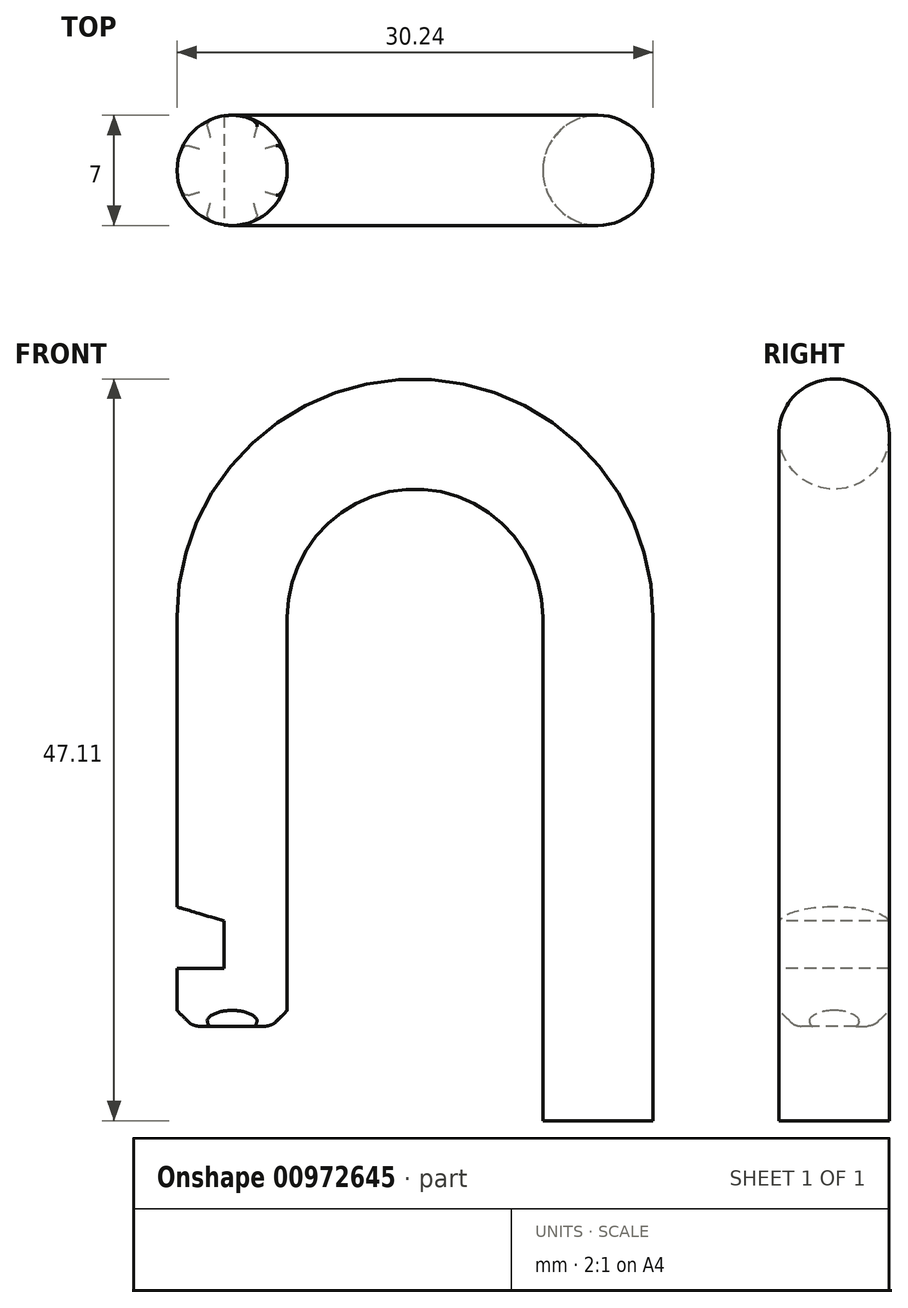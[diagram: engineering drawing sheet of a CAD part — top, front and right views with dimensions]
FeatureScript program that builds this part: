
annotation { "Feature Type Name" : "Feature", "Feature Type Description" : "" }
export const myFeature = defineFeature(function(context is Context, id is Id, definition is map)
    precondition{}
    {
        {
            var Q0;
            Q0=qCreatedBy(makeId("Front.planeOp"),FACE);
            var sketch = newSketch(context, id + "F0", { "sketchPlane" : qUnion([Q0])});
            skArc(sketch, "E0", {"start": v(8.12, 0) * mm, "mid": v(0, 8.12) * mm, "end": v(-8.12, 0) * mm});
            skLineSegment(sketch, "E1", {"start": v(15.12, 0) * mm, "end": v(15.12, -32) * mm});
            skLineSegment(sketch, "E2", {"start": v(-15.12, 0) * mm, "end": v(-15.11, -18.42) * mm});
            skArc(sketch, "E3", {"start": v(15.12, 0) * mm, "mid": v(0, 15.12) * mm, "end": v(-15.12, 0) * mm});
            skLineSegment(sketch, "E4.trimOffspring", {"start": v(-8.12, 0) * mm, "end": v(-8.11, -25) * mm});
            skLineSegment(sketch, "E5.trimOffspring", {"start": v(8.12, 0) * mm, "end": v(8.12, -32) * mm});
            skLineSegment(sketch, "E6", {"start": v(8.12, -32) * mm, "end": v(15.12, -32) * mm});
            skLineSegment(sketch, "E7.top", {"start": v(-12.11, -22.32) * mm, "end": v(-15.11, -22.32) * mm});
            skLineSegment(sketch, "E7.left", {"start": v(-12.11, -19.32) * mm, "end": v(-12.11, -22.32) * mm});
            skLineSegment(sketch, "E8", {"start": v(-12.11, -19.32) * mm, "end": v(-15.11, -18.42) * mm});
            skLineSegment(sketch, "E9.bottom", {"start": v(-15.11, -25) * mm, "end": v(-8.11, -25) * mm});
            skLineSegment(sketch, "E9.top", {"start": v(-15.11, -26) * mm, "end": v(-8.11, -26) * mm});
            skLineSegment(sketch, "E9.left", {"start": v(-15.11, -25) * mm, "end": v(-15.11, -26) * mm});
            skLineSegment(sketch, "E9.right", {"start": v(-8.11, -25) * mm, "end": v(-8.11, -26) * mm});
            skLineSegment(sketch, "E10.trimOffspring", {"start": v(-15.11, -22.32) * mm, "end": v(-15.11, -25) * mm});
            skSolve(sketch);
        }
        {
            var Q0;
            Q0 = qSketchRegion(id + "F0", true);
            extrude(context, id + "F1", {"entities" : qUnion([Q0]), "oppositeDirection" : true, "depth" : 7 * mm, "offsetDistance" : 25 * mm});
        }
        {
            var Q0;
            Q0=makeQuery(id+"F1.opExtrude","SWEPT_EDGE",EDGE,{"disambiguationData":[OSD([sQuery(id+"F0.wireOp",EDGE,"E9.top"),sQuery(id+"F0.wireOp",EDGE,"E9.right")])]});
            var Q1;
            Q1=makeQuery(id+"F1.opExtrude","CAP_EDGE",EDGE,{"disambiguationData":[OSD([sQuery(id+"F0.wireOp",EDGE,"E9.top")])],"isStart":true});
            var Q2;
            Q2=makeQuery(id+"F1.opExtrude","CAP_EDGE",EDGE,{"disambiguationData":[OSD([sQuery(id+"F0.wireOp",EDGE,"E9.top")])],"isStart":false});
            var Q3;
            Q3=makeQuery(id+"F1.opExtrude","SWEPT_EDGE",EDGE,{"disambiguationData":[OSD([sQuery(id+"F0.wireOp",EDGE,"E9.top"),sQuery(id+"F0.wireOp",EDGE,"E9.left")])]});
            chamfer(context, id + "F2", {"entities" : qUnion([Q0, Q1, Q2, Q3]), "width" : 1 * mm, "tangentPropagation" : true});
        }
        {
            var Q0;
            Q0=makeQuery(id+"F1.opExtrude","CAP_EDGE",EDGE,{"disambiguationData":[OSD([sQuery(id+"F0.wireOp",EDGE,"E5.trimOffspring")])],"isStart":true});
            var Q1;
            Q1=makeQuery(id+"F1.opExtrude","CAP_EDGE",EDGE,{"disambiguationData":[OSD([sQuery(id+"F0.wireOp",EDGE,"E1")])],"isStart":true});
            var Q2;
            Q2=makeQuery(id+"F1.opExtrude","CAP_EDGE",EDGE,{"disambiguationData":[OSD([sQuery(id+"F0.wireOp",EDGE,"E1")])],"isStart":false});
            var Q3;
            Q3=makeQuery(id+"F1.opExtrude","CAP_EDGE",EDGE,{"disambiguationData":[OSD([sQuery(id+"F0.wireOp",EDGE,"E5.trimOffspring")])],"isStart":false});
            fillet(context, id + "F3", {"entities" : qUnion([Q0, Q1, Q2, Q3]), "radius" : 3.5 * mm, "tangentPropagation" : true, "allowEdgeOverflow" : false});
        }
        {
            var Q0;
            {var subQ0=sQuery(id+"F0.wireOp",EDGE,"E9.top");Q0=makeQuery(id+"F2.opChamfer","BLEND_EDGE",EDGE,{"blendedFrom":[makeQuery(id+"F1.opExtrude","CAP_EDGE",EDGE,{"disambiguationData":[OSD([subQ0])],"isStart":false}),makeQuery(id+"F1.opExtrude","SWEPT_FACE",FACE,{"disambiguationData":[OSD([subQ0])]})],"blendedInto":[makeQuery(id+"F1.opExtrude","SWEPT_FACE",FACE,{"disambiguationData":[OSD([subQ0])]})]});}
            var Q1;
            {var subQ0=sQuery(id+"F0.wireOp",EDGE,"E9.top");Q1=makeQuery(id+"F2.opChamfer","BLEND_EDGE",EDGE,{"blendedFrom":[makeQuery(id+"F1.opExtrude","SWEPT_EDGE",EDGE,{"disambiguationData":[OSD([subQ0,sQuery(id+"F0.wireOp",EDGE,"E9.left")])]}),makeQuery(id+"F1.opExtrude","SWEPT_FACE",FACE,{"disambiguationData":[OSD([subQ0])]})],"blendedInto":[makeQuery(id+"F1.opExtrude","SWEPT_FACE",FACE,{"disambiguationData":[OSD([subQ0])]})]});}
            var Q2;
            {var subQ0=sQuery(id+"F0.wireOp",EDGE,"E9.top");Q2=makeQuery(id+"F2.opChamfer","BLEND_EDGE",EDGE,{"blendedFrom":[makeQuery(id+"F1.opExtrude","CAP_EDGE",EDGE,{"disambiguationData":[OSD([subQ0])],"isStart":true}),makeQuery(id+"F1.opExtrude","SWEPT_FACE",FACE,{"disambiguationData":[OSD([subQ0])]})],"blendedInto":[makeQuery(id+"F1.opExtrude","SWEPT_FACE",FACE,{"disambiguationData":[OSD([subQ0])]})]});}
            var Q3;
            Q3=makeQuery(id+"F1.opExtrude","SWEPT_FACE",FACE,{"disambiguationData":[OSD([sQuery(id+"F0.wireOp",EDGE,"E9.top")])]});
            fillet(context, id + "F4", {"entities" : qUnion([Q0, Q1, Q2, Q3]), "radius" : 1 * mm, "tangentPropagation" : true, "allowEdgeOverflow" : false});
        }
    });
